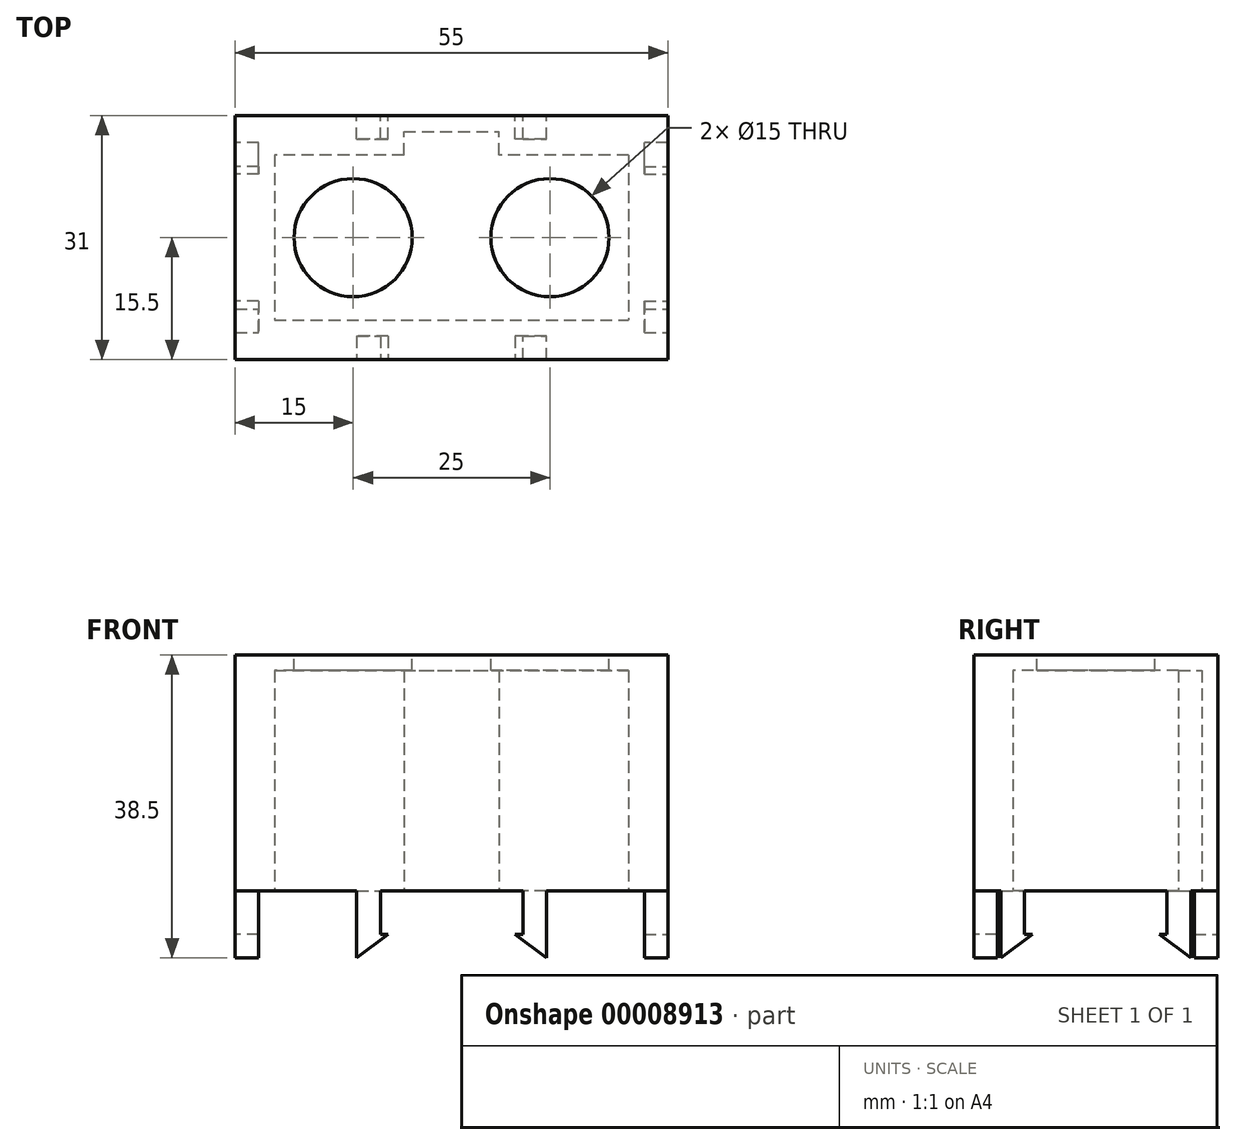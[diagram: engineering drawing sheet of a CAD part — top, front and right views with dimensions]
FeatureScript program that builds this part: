
annotation { "Feature Type Name" : "Feature", "Feature Type Description" : "" }
export const myFeature = defineFeature(function(context is Context, id is Id, definition is map)
    precondition{}
    {
        {
            var Q0;
            Q0=qCreatedBy(makeId("Top.planeOp"),FACE);
            var sketch = newSketch(context, id + "F0", { "sketchPlane" : qUnion([Q0])});
            skLineSegment(sketch, "E0", {"start": v(0, 0) * mm, "end": v(-22, 0) * mm});
            skLineSegment(sketch, "E1", {"start": v(0, 0) * mm, "end": v(22, 0) * mm});
            skLineSegment(sketch, "E2.0", {"start": v(0, 10) * mm, "end": v(-22, 10) * mm, "construction": true});
            skLineSegment(sketch, "E3.0", {"start": v(0, 10) * mm, "end": v(22, 10) * mm, "construction": true});
            skLineSegment(sketch, "E4.0", {"start": v(0, -10) * mm, "end": v(22, -10) * mm, "construction": true});
            skLineSegment(sketch, "E5.0", {"start": v(0, -10) * mm, "end": v(-22, -10) * mm, "construction": true});
            skLineSegment(sketch, "E6", {"start": v(-22, 10) * mm, "end": v(-22, -10) * mm, "construction": true});
            skLineSegment(sketch, "E7", {"start": v(22, 10) * mm, "end": v(22, -10) * mm, "construction": true});
            skLineSegment(sketch, "E8.0", {"start": v(0, 10.5) * mm, "end": v(-22.5, 10.5) * mm});
            skLineSegment(sketch, "E9.0", {"start": v(0, 10.5) * mm, "end": v(23.37, 10.5) * mm});
            skLineSegment(sketch, "E10.0", {"start": v(-22.5, 12.52) * mm, "end": v(-22.5, -12.38) * mm});
            skLineSegment(sketch, "E11.0", {"start": v(22.5, 10.5) * mm, "end": v(22.5, -10.5) * mm});
            skLineSegment(sketch, "E12.0", {"start": v(0, -10.5) * mm, "end": v(23.75, -10.5) * mm});
            skLineSegment(sketch, "E13.0", {"start": v(0, -10.5) * mm, "end": v(-22.5, -10.5) * mm});
            skLineSegment(sketch, "E14.0", {"start": v(-27.5, 15.5) * mm, "end": v(-27.5, -18.22) * mm});
            skLineSegment(sketch, "E15.0", {"start": v(0, 15.5) * mm, "end": v(-27.5, 15.5) * mm});
            skLineSegment(sketch, "E16.0", {"start": v(0, 15.5) * mm, "end": v(27.5, 15.5) * mm});
            skLineSegment(sketch, "E17.0", {"start": v(27.5, 15.5) * mm, "end": v(27.5, -15.5) * mm});
            skLineSegment(sketch, "E18.0", {"start": v(0, -15.5) * mm, "end": v(27.5, -15.5) * mm});
            skLineSegment(sketch, "E19.0", {"start": v(0, -15.5) * mm, "end": v(-27.5, -15.5) * mm});
            skSolve(sketch);
        }
        {
            var Q0;
            {var subQ7=sQuery(id+"F0.wireOp",EDGE,"E8.0");Q0=makeQuery(id+"F0.imprint","IMPRINT",FACE,{"disambiguationData":[TD([[makeQuery(id+"F0.imprint","IMPRINT",EDGE,{"derivedFrom":subQ7}),-1.0]])]});}
            extrude(context, id + "F1", {"entities" : qUnion([Q0]), "depth" : 30 * mm});
        }
        {
            var Q0;
            Q0=makeQuery(id+"F1.opExtrude","CAP_FACE",FACE,{"disambiguationData":[OSD([sQuery(id+"F0.wireOp",EDGE,"E8.0"),sQuery(id+"F0.wireOp",EDGE,"E9.0"),sQuery(id+"F0.wireOp",EDGE,"E10.0"),sQuery(id+"F0.wireOp",EDGE,"E11.0"),sQuery(id+"F0.wireOp",EDGE,"E12.0"),sQuery(id+"F0.wireOp",EDGE,"E13.0"),sQuery(id+"F0.wireOp",EDGE,"E14.0"),sQuery(id+"F0.wireOp",EDGE,"E15.0"),sQuery(id+"F0.wireOp",EDGE,"E16.0"),sQuery(id+"F0.wireOp",EDGE,"E17.0"),sQuery(id+"F0.wireOp",EDGE,"E18.0"),sQuery(id+"F0.wireOp",EDGE,"E19.0")])],"isStart":false});
            var sketch = newSketch(context, id + "F2", { "sketchPlane" : qUnion([Q0])});
            skLineSegment(sketch, "E20", {"start": v(-22.5, 10.5) * mm, "end": v(-22.5, -10.5) * mm});
            skLineSegment(sketch, "E21", {"start": v(-22.5, -10.5) * mm, "end": v(22.5, -10.5) * mm});
            skLineSegment(sketch, "E22", {"start": v(22.5, -10.5) * mm, "end": v(22.5, 10.5) * mm});
            skLineSegment(sketch, "E23", {"start": v(22.5, 10.5) * mm, "end": v(-22.5, 10.5) * mm});
            skSolve(sketch);
        }
        {
            var Q0;
            Q0=makeQuery(id+"F2.imprint","IMPRINT",FACE,{"disambiguationData":[TD([[makeQuery(id+"F2.imprint","IMPRINT",EDGE,{"derivedFrom":sQuery(id+"F2.wireOp",EDGE,"E20")}),1.0]])]});
            extrude(context, id + "F3", {"entities" : qUnion([Q0]), "operationType" : NewBodyOperationType.ADD, "oppositeDirection" : true, "depth" : 2 * mm});
        }
        {
            var Q0;
            {var subQ7=sQuery(id+"F0.wireOp",EDGE,"E8.0");Q0=makeQuery(id+"F0.imprint","IMPRINT",FACE,{"disambiguationData":[TD([[makeQuery(id+"F0.imprint","IMPRINT",EDGE,{"derivedFrom":subQ7}),-1.0]])]});}
            var sketch = newSketch(context, id + "F4", { "sketchPlane" : qUnion([Q0])});
            skLineSegment(sketch, "E24.0", {"start": v(0, 10.5) * mm, "end": v(-22.5, 10.5) * mm});
            skLineSegment(sketch, "E25.0", {"start": v(0, 10.5) * mm, "end": v(23.37, 10.5) * mm});
            skLineSegment(sketch, "E26", {"start": v(0, 10.5) * mm, "end": v(0, 13.5) * mm});
            skPoint(sketch, "E27.orphan", {"position": v(0, 12.52) * mm});
            skLineSegment(sketch, "E28.0", {"start": v(6.05, 10.5) * mm, "end": v(6.05, 13.5) * mm});
            skLineSegment(sketch, "E29.0", {"start": v(-6.05, 10.5) * mm, "end": v(-6.05, 13.5) * mm});
            skLineSegment(sketch, "E30", {"start": v(-6.05, 13.5) * mm, "end": v(6.05, 13.5) * mm});
            skSolve(sketch);
        }
        {
            var Q0;
            {var subQ2=sQuery(id+"F4.wireOp",EDGE,"E26");Q0=makeQuery(id+"F4.imprint","IMPRINT",FACE,{"disambiguationData":[TD([[makeQuery(id+"F4.imprint","IMPRINT",EDGE,{"derivedFrom":subQ2}),1.0]])]});}
            var Q1;
            {var subQ2=sQuery(id+"F4.wireOp",EDGE,"E26");Q1=makeQuery(id+"F4.imprint","IMPRINT",FACE,{"disambiguationData":[TD([[makeQuery(id+"F4.imprint","IMPRINT",EDGE,{"derivedFrom":subQ2}),-1.0]])]});}
            extrude(context, id + "F5", {"entities" : qUnion([Q0, Q1]), "operationType" : NewBodyOperationType.REMOVE, "depth" : 28 * mm});
        }
        {
            var Q0;
            Q0=makeQuery(id+"F3.boolean.opBoolean","MERGE",FACE,{"derivedFrom":[makeQuery(id+"F1.opExtrude","CAP_FACE",FACE,{"disambiguationData":[OSD([sQuery(id+"F0.wireOp",EDGE,"E8.0"),sQuery(id+"F0.wireOp",EDGE,"E9.0"),sQuery(id+"F0.wireOp",EDGE,"E10.0"),sQuery(id+"F0.wireOp",EDGE,"E11.0"),sQuery(id+"F0.wireOp",EDGE,"E12.0"),sQuery(id+"F0.wireOp",EDGE,"E13.0"),sQuery(id+"F0.wireOp",EDGE,"E14.0"),sQuery(id+"F0.wireOp",EDGE,"E15.0"),sQuery(id+"F0.wireOp",EDGE,"E16.0"),sQuery(id+"F0.wireOp",EDGE,"E17.0"),sQuery(id+"F0.wireOp",EDGE,"E18.0"),sQuery(id+"F0.wireOp",EDGE,"E19.0")])],"isStart":false}),makeQuery(id+"F3.opExtrude","CAP_FACE",FACE,{"disambiguationData":[OSD([sQuery(id+"F2.wireOp",EDGE,"E20"),sQuery(id+"F2.wireOp",EDGE,"E21"),sQuery(id+"F2.wireOp",EDGE,"E22"),sQuery(id+"F2.wireOp",EDGE,"E23")])],"isStart":true})]});
            var sketch = newSketch(context, id + "F6", { "sketchPlane" : qUnion([Q0])});
            skLineSegment(sketch, "E31", {"start": v(0, 0) * mm, "end": v(-5, 0) * mm});
            skLineSegment(sketch, "E32", {"start": v(0, 0) * mm, "end": v(5, 0) * mm});
            skLineSegment(sketch, "E33", {"start": v(-5, 0) * mm, "end": v(-12.5, 0) * mm});
            skLineSegment(sketch, "E34", {"start": v(5, 0) * mm, "end": v(12.5, 0) * mm});
            skCircle(sketch, "E35", {"center": v(-12.5, 0) * mm, "radius": 7.5 * mm});
            skCircle(sketch, "E36", {"center": v(12.5, 0) * mm, "radius": 7.5 * mm});
            skSolve(sketch);
        }
        {
            var Q0;
            Q0=makeQuery(id+"F6.imprint","IMPRINT",FACE,{"disambiguationData":[TD([[makeQuery(id+"F6.imprint","IMPRINT",EDGE,{"derivedFrom":sQuery(id+"F6.wireOp",EDGE,"E35")}),1.0]])]});
            var Q1;
            Q1=makeQuery(id+"F6.imprint","IMPRINT",FACE,{"disambiguationData":[TD([[makeQuery(id+"F6.imprint","IMPRINT",EDGE,{"derivedFrom":sQuery(id+"F6.wireOp",EDGE,"E36")}),1.0]])]});
            extrude(context, id + "F7", {"entities" : qUnion([Q0, Q1]), "operationType" : NewBodyOperationType.REMOVE, "oppositeDirection" : true, "depth" : 2 * mm});
        }
        {
            var Q0;
            Q0=makeQuery(id+"F1.opExtrude","CAP_FACE",FACE,{"disambiguationData":[OSD([sQuery(id+"F0.wireOp",EDGE,"E8.0"),sQuery(id+"F0.wireOp",EDGE,"E9.0"),sQuery(id+"F0.wireOp",EDGE,"E10.0"),sQuery(id+"F0.wireOp",EDGE,"E11.0"),sQuery(id+"F0.wireOp",EDGE,"E12.0"),sQuery(id+"F0.wireOp",EDGE,"E13.0"),sQuery(id+"F0.wireOp",EDGE,"E14.0"),sQuery(id+"F0.wireOp",EDGE,"E15.0"),sQuery(id+"F0.wireOp",EDGE,"E16.0"),sQuery(id+"F0.wireOp",EDGE,"E17.0"),sQuery(id+"F0.wireOp",EDGE,"E18.0"),sQuery(id+"F0.wireOp",EDGE,"E19.0")])],"isStart":true});
            var sketch = newSketch(context, id + "F8", { "sketchPlane" : qUnion([Q0])});
            skLineSegment(sketch, "E37", {"start": v(0, 0) * mm, "end": v(-27.5, 0) * mm});
            skLineSegment(sketch, "E38", {"start": v(0, 0) * mm, "end": v(27.5, 0) * mm});
            skLineSegment(sketch, "E39", {"start": v(0, 0) * mm, "end": v(0, 15.5) * mm});
            skLineSegment(sketch, "E40", {"start": v(0, 0) * mm, "end": v(0, -15.5) * mm});
            skLineSegment(sketch, "E41", {"start": v(-27.5, 0) * mm, "end": v(-27.5, 9.05) * mm});
            skLineSegment(sketch, "E42", {"start": v(-27.5, 0) * mm, "end": v(-27.5, -9.05) * mm});
            skLineSegment(sketch, "E43", {"start": v(0, 15.5) * mm, "end": v(9.05, 15.5) * mm});
            skLineSegment(sketch, "E44", {"start": v(0, 15.5) * mm, "end": v(-9.05, 15.5) * mm});
            skLineSegment(sketch, "E45", {"start": v(27.5, 0) * mm, "end": v(27.5, 9.05) * mm});
            skLineSegment(sketch, "E46", {"start": v(27.5, 0) * mm, "end": v(27.5, -9.05) * mm});
            skLineSegment(sketch, "E47", {"start": v(0, -15.5) * mm, "end": v(9.05, -15.5) * mm});
            skLineSegment(sketch, "E48", {"start": v(0, -15.5) * mm, "end": v(-9.05, -15.5) * mm});
            skPoint(sketch, "E49.orphan", {"position": v(6.05, -15.5) * mm});
            skLineSegment(sketch, "E50.0", {"start": v(24.5, 0) * mm, "end": v(24.5, -9.05) * mm});
            skLineSegment(sketch, "E50.1", {"start": v(24.5, 0) * mm, "end": v(24.5, 9.05) * mm});
            skLineSegment(sketch, "E51.0", {"start": v(0, -12.5) * mm, "end": v(9.05, -12.5) * mm});
            skLineSegment(sketch, "E51.1", {"start": v(0, -12.5) * mm, "end": v(-9.05, -12.5) * mm});
            skLineSegment(sketch, "E52.0", {"start": v(-24.5, 0) * mm, "end": v(-24.5, 9.05) * mm});
            skLineSegment(sketch, "E52.1", {"start": v(-24.5, 0) * mm, "end": v(-24.5, -9.05) * mm});
            skLineSegment(sketch, "E53.0", {"start": v(0, 12.5) * mm, "end": v(-9.05, 12.5) * mm});
            skLineSegment(sketch, "E53.1", {"start": v(0, 12.5) * mm, "end": v(9.05, 12.5) * mm});
            skLineSegment(sketch, "E54", {"start": v(-27.5, 9.05) * mm, "end": v(-24.5, 9.05) * mm});
            skLineSegment(sketch, "E55", {"start": v(-24.5, -9.05) * mm, "end": v(-27.5, -9.05) * mm});
            skLineSegment(sketch, "E56", {"start": v(-9.05, 12.5) * mm, "end": v(-9.05, 15.5) * mm});
            skLineSegment(sketch, "E57", {"start": v(9.05, 15.5) * mm, "end": v(9.05, 12.5) * mm});
            skLineSegment(sketch, "E58", {"start": v(24.5, 9.05) * mm, "end": v(27.5, 9.05) * mm});
            skLineSegment(sketch, "E59", {"start": v(27.5, -9.05) * mm, "end": v(24.5, -9.05) * mm});
            skLineSegment(sketch, "E60", {"start": v(9.05, -12.5) * mm, "end": v(9.05, -15.5) * mm});
            skLineSegment(sketch, "E61", {"start": v(-9.05, -12.5) * mm, "end": v(-9.05, -15.5) * mm});
            skLineSegment(sketch, "E62.0", {"start": v(-24.5, -12.05) * mm, "end": v(-27.5, -12.05) * mm});
            skLineSegment(sketch, "E63.0", {"start": v(-27.5, 12.05) * mm, "end": v(-24.5, 12.05) * mm});
            skLineSegment(sketch, "E64.0", {"start": v(-12.05, 12.5) * mm, "end": v(-12.05, 15.5) * mm});
            skLineSegment(sketch, "E65.0", {"start": v(12.05, 15.5) * mm, "end": v(12.05, 12.5) * mm});
            skLineSegment(sketch, "E66.0", {"start": v(24.5, 12.05) * mm, "end": v(27.5, 12.05) * mm});
            skLineSegment(sketch, "E67.0", {"start": v(27.5, -12.05) * mm, "end": v(24.5, -12.05) * mm});
            skLineSegment(sketch, "E68.0", {"start": v(12.05, -12.5) * mm, "end": v(12.05, -15.5) * mm});
            skLineSegment(sketch, "E69.0", {"start": v(-12.05, -12.5) * mm, "end": v(-12.05, -15.5) * mm});
            skLineSegment(sketch, "E70", {"start": v(-24.5, -9.05) * mm, "end": v(-24.5, -12.05) * mm});
            skLineSegment(sketch, "E71", {"start": v(-27.5, -9.05) * mm, "end": v(-27.5, -12.05) * mm});
            skLineSegment(sketch, "E72", {"start": v(-27.5, 12.05) * mm, "end": v(-27.5, 9.05) * mm});
            skLineSegment(sketch, "E73", {"start": v(-24.5, 12.05) * mm, "end": v(-24.5, 9.05) * mm});
            skLineSegment(sketch, "E74", {"start": v(-12.05, 15.5) * mm, "end": v(-9.05, 15.5) * mm});
            skLineSegment(sketch, "E75", {"start": v(-12.05, 12.5) * mm, "end": v(-9.05, 12.5) * mm});
            skLineSegment(sketch, "E76", {"start": v(9.05, 15.5) * mm, "end": v(12.05, 15.5) * mm});
            skLineSegment(sketch, "E77", {"start": v(9.05, 12.5) * mm, "end": v(12.05, 12.5) * mm});
            skLineSegment(sketch, "E78", {"start": v(24.5, 12.05) * mm, "end": v(24.5, 9.05) * mm});
            skLineSegment(sketch, "E79", {"start": v(27.5, 12.05) * mm, "end": v(27.5, 9.05) * mm});
            skLineSegment(sketch, "E80", {"start": v(24.5, -9.05) * mm, "end": v(24.5, -12.05) * mm});
            skLineSegment(sketch, "E81", {"start": v(27.5, -9.05) * mm, "end": v(27.5, -12.05) * mm});
            skLineSegment(sketch, "E82", {"start": v(9.05, -12.5) * mm, "end": v(12.05, -12.5) * mm});
            skLineSegment(sketch, "E83", {"start": v(9.05, -15.5) * mm, "end": v(12.05, -15.5) * mm});
            skLineSegment(sketch, "E84", {"start": v(-12.05, -12.5) * mm, "end": v(-9.05, -12.5) * mm});
            skLineSegment(sketch, "E85", {"start": v(-12.05, -15.5) * mm, "end": v(-9.05, -15.5) * mm});
            skSolve(sketch);
        }
        {
            var Q0;
            Q0=makeQuery(id+"F8.imprint","IMPRINT",FACE,{"disambiguationData":[TD([[makeQuery(id+"F8.imprint","IMPRINT",EDGE,{"derivedFrom":sQuery(id+"F8.wireOp",EDGE,"E54")}),1.0]])]});
            var Q1;
            Q1=makeQuery(id+"F8.imprint","IMPRINT",FACE,{"disambiguationData":[TD([[makeQuery(id+"F8.imprint","IMPRINT",EDGE,{"derivedFrom":sQuery(id+"F8.wireOp",EDGE,"E55")}),1.0]])]});
            var Q2;
            Q2=makeQuery(id+"F8.imprint","IMPRINT",FACE,{"disambiguationData":[TD([[makeQuery(id+"F8.imprint","IMPRINT",EDGE,{"derivedFrom":sQuery(id+"F8.wireOp",EDGE,"E61")}),-1.0]])]});
            var Q3;
            Q3=makeQuery(id+"F8.imprint","IMPRINT",FACE,{"disambiguationData":[TD([[makeQuery(id+"F8.imprint","IMPRINT",EDGE,{"derivedFrom":sQuery(id+"F8.wireOp",EDGE,"E60")}),1.0]])]});
            var Q4;
            Q4=makeQuery(id+"F8.imprint","IMPRINT",FACE,{"disambiguationData":[TD([[makeQuery(id+"F8.imprint","IMPRINT",EDGE,{"derivedFrom":sQuery(id+"F8.wireOp",EDGE,"E56")}),1.0]])]});
            var Q5;
            Q5=makeQuery(id+"F8.imprint","IMPRINT",FACE,{"disambiguationData":[TD([[makeQuery(id+"F8.imprint","IMPRINT",EDGE,{"derivedFrom":sQuery(id+"F8.wireOp",EDGE,"E57")}),1.0]])]});
            var Q6;
            Q6=makeQuery(id+"F8.imprint","IMPRINT",FACE,{"disambiguationData":[TD([[makeQuery(id+"F8.imprint","IMPRINT",EDGE,{"derivedFrom":sQuery(id+"F8.wireOp",EDGE,"E58")}),1.0]])]});
            var Q7;
            Q7=makeQuery(id+"F8.imprint","IMPRINT",FACE,{"disambiguationData":[TD([[makeQuery(id+"F8.imprint","IMPRINT",EDGE,{"derivedFrom":sQuery(id+"F8.wireOp",EDGE,"E59")}),1.0]])]});
            extrude(context, id + "F9", {"entities" : qUnion([Q0, Q1, Q2, Q3, Q4, Q5, Q6, Q7]), "operationType" : NewBodyOperationType.ADD, "depth" : 8.5 * mm});
        }
        {
            var Q0;
            Q0=makeQuery(id+"F9.boolean.opBoolean","MERGE",FACE,{"derivedFrom":[makeQuery(id+"F1.opExtrude","SWEPT_FACE",FACE,{"disambiguationData":[OSD([sQuery(id+"F0.wireOp",EDGE,"E14.0")])]}),makeQuery(id+"F9.opExtrude","SWEPT_FACE",FACE,{"disambiguationData":[OSD([sQuery(id+"F8.wireOp",EDGE,"E71")])]}),makeQuery(id+"F9.opExtrude","SWEPT_FACE",FACE,{"disambiguationData":[OSD([sQuery(id+"F8.wireOp",EDGE,"E72")])]})]});
            var sketch = newSketch(context, id + "F10", { "sketchPlane" : qUnion([Q0])});
            skLineSegment(sketch, "E86.0", {"start": v(9.05, -6.5) * mm, "end": v(12.05, -6.5) * mm, "construction": true});
            skLineSegment(sketch, "E87.0", {"start": v(8.05, -5.5) * mm, "end": v(12.05, -5.5) * mm});
            skLineSegment(sketch, "E88.0", {"start": v(-12.05, -6.5) * mm, "end": v(-9.05, -6.5) * mm, "construction": true});
            skLineSegment(sketch, "E89.0", {"start": v(-12.05, -5.5) * mm, "end": v(-8.05, -5.5) * mm});
            skLineSegment(sketch, "E90.0", {"start": v(8.05, -8.5) * mm, "end": v(8.05, 0) * mm});
            skLineSegment(sketch, "E91.0", {"start": v(-8.05, -8.5) * mm, "end": v(-8.05, 0) * mm});
            skLineSegment(sketch, "E92", {"start": v(12.05, -8.5) * mm, "end": v(8.05, -5.5) * mm});
            skLineSegment(sketch, "E93", {"start": v(-12.05, -8.5) * mm, "end": v(-8.05, -5.5) * mm});
            skSolve(sketch);
        }
        {
            var Q0;
            {var subQ0=sQuery(id+"F8.wireOp",EDGE,"E72");var subQ4=makeQuery(id+"F9.opExtrude","CAP_EDGE",EDGE,{"disambiguationData":[OSD([subQ0])],"isStart":false});Q0=makeQuery(id+"F10.imprint","IMPRINT",FACE,{"disambiguationData":[TD([[makeQuery(id+"F10.imprint","IMPRINT",EDGE,{"derivedFrom":subQ4}),1.0]])]});}
            var Q1;
            {var subQ0=sQuery(id+"F8.wireOp",EDGE,"E71");var subQ4=makeQuery(id+"F9.opExtrude","CAP_EDGE",EDGE,{"disambiguationData":[OSD([subQ0])],"isStart":false});Q1=makeQuery(id+"F10.imprint","IMPRINT",FACE,{"disambiguationData":[TD([[makeQuery(id+"F10.imprint","IMPRINT",EDGE,{"derivedFrom":subQ4}),1.0]])]});}
            extrude(context, id + "F11", {"entities" : qUnion([Q0, Q1]), "operationType" : NewBodyOperationType.REMOVE, "oppositeDirection" : true, "depth" : 60 * mm});
        }
        {
            var Q0;
            {var subQ1=sQuery(id+"F10.wireOp",EDGE,"E87.0");var subQ3=sQuery(id+"F10.wireOp",EDGE,"E92");var subQ5=makeQuery(id+"F10.imprint","INTERSECT",VERTEX,{"derivedFrom":[subQ1,sQuery(id+"F10.wireOp",EDGE,"E90.0"),subQ3]});Q0=makeQuery(id+"F10.imprint","IMPRINT",FACE,{"disambiguationData":[TD([[makeQuery(id+"F10.imprint","IMPRINT",EDGE,{"disambiguationData":[TD([[subQ5,-1.0]])],"derivedFrom":subQ1}),-1.0]])]});}
            var Q1;
            {var subQ1=sQuery(id+"F10.wireOp",EDGE,"E89.0");var subQ3=sQuery(id+"F10.wireOp",EDGE,"E93");var subQ5=makeQuery(id+"F10.imprint","INTERSECT",VERTEX,{"derivedFrom":[subQ1,sQuery(id+"F10.wireOp",EDGE,"E91.0"),subQ3]});Q1=makeQuery(id+"F10.imprint","IMPRINT",FACE,{"disambiguationData":[TD([[makeQuery(id+"F10.imprint","IMPRINT",EDGE,{"disambiguationData":[TD([[subQ5,1.0]])],"derivedFrom":subQ1}),-1.0]])]});}
            extrude(context, id + "F12", {"entities" : qUnion([Q0, Q1]), "operationType" : NewBodyOperationType.ADD, "oppositeDirection" : true, "depth" : 3 * mm});
        }
        {
            var Q0;
            Q0=makeQuery(id+"F9.boolean.opBoolean","MERGE",FACE,{"derivedFrom":[makeQuery(id+"F1.opExtrude","SWEPT_FACE",FACE,{"disambiguationData":[OSD([sQuery(id+"F0.wireOp",EDGE,"E17.0")])]}),makeQuery(id+"F9.opExtrude","SWEPT_FACE",FACE,{"disambiguationData":[OSD([sQuery(id+"F8.wireOp",EDGE,"E79")])]}),makeQuery(id+"F9.opExtrude","SWEPT_FACE",FACE,{"disambiguationData":[OSD([sQuery(id+"F8.wireOp",EDGE,"E81")])]})]});
            var sketch = newSketch(context, id + "F13", { "sketchPlane" : qUnion([Q0])});
            skLineSegment(sketch, "E94", {"start": v(12.05, -8.5) * mm, "end": v(7.95, -8.5) * mm});
            skLineSegment(sketch, "E95.0", {"start": v(8.05, -8.5) * mm, "end": v(8.05, 0) * mm});
            skLineSegment(sketch, "E96.0", {"start": v(9.05, -8.5) * mm, "end": v(9.05, 0) * mm});
            skLineSegment(sketch, "E97.0", {"start": v(12.05, -5.5) * mm, "end": v(8.05, -5.5) * mm});
            skLineSegment(sketch, "E98", {"start": v(12.05, -8.5) * mm, "end": v(8.05, -5.5) * mm});
            skLineSegment(sketch, "E99", {"start": v(-12.05, -8.5) * mm, "end": v(-7.05, -8.5) * mm});
            skLineSegment(sketch, "E100.0", {"start": v(-8.05, -6.25) * mm, "end": v(-8.05, 0) * mm});
            skLineSegment(sketch, "E101.0", {"start": v(-9.05, -6.25) * mm, "end": v(-9.05, 0) * mm});
            skLineSegment(sketch, "E102.0", {"start": v(-12.05, -5.5) * mm, "end": v(-8.05, -5.5) * mm});
            skLineSegment(sketch, "E103", {"start": v(-12.05, -8.5) * mm, "end": v(-8.05, -5.5) * mm});
            skSolve(sketch);
        }
        {
            var Q0;
            {var subQ0=sQuery(id+"F13.wireOp",EDGE,"E98");var subQ3=sQuery(id+"F13.wireOp",EDGE,"E96.0");var subQ4=makeQuery(id+"F13.imprint","INTERSECT",VERTEX,{"derivedFrom":[subQ3,subQ0]});Q0=makeQuery(id+"F13.imprint","IMPRINT",FACE,{"disambiguationData":[TD([[makeQuery(id+"F13.imprint","IMPRINT",EDGE,{"disambiguationData":[TD([[subQ4,-1.0]])],"derivedFrom":subQ3}),1.0]])]});}
            var Q1;
            {var subQ0=sQuery(id+"F13.wireOp",EDGE,"E103");var subQ3=sQuery(id+"F13.wireOp",EDGE,"E101.0");var subQ4=makeQuery(id+"F13.imprint","INTERSECT",VERTEX,{"derivedFrom":[subQ3,subQ0]});Q1=makeQuery(id+"F13.imprint","IMPRINT",FACE,{"disambiguationData":[TD([[makeQuery(id+"F13.imprint","IMPRINT",EDGE,{"disambiguationData":[TD([[subQ4,-1.0]])],"derivedFrom":subQ3}),-1.0]])]});}
            extrude(context, id + "F14", {"entities" : qUnion([Q0, Q1]), "operationType" : NewBodyOperationType.ADD, "oppositeDirection" : true, "depth" : 3 * mm});
        }
        {
            var Q0;
            Q0=makeQuery(id+"F9.boolean.opBoolean","MERGE",FACE,{"derivedFrom":[makeQuery(id+"F1.opExtrude","SWEPT_FACE",FACE,{"disambiguationData":[OSD([sQuery(id+"F0.wireOp",EDGE,"E18.0"),sQuery(id+"F0.wireOp",EDGE,"E19.0")])]}),makeQuery(id+"F9.opExtrude","SWEPT_FACE",FACE,{"disambiguationData":[OSD([sQuery(id+"F8.wireOp",EDGE,"E74")])]}),makeQuery(id+"F9.opExtrude","SWEPT_FACE",FACE,{"disambiguationData":[OSD([sQuery(id+"F8.wireOp",EDGE,"E76")])]})]});
            var sketch = newSketch(context, id + "F15", { "sketchPlane" : qUnion([Q0])});
            skLineSegment(sketch, "E104.0", {"start": v(12.05, -6.5) * mm, "end": v(9.05, -6.5) * mm, "construction": true});
            skLineSegment(sketch, "E105.0", {"start": v(12.05, -5.5) * mm, "end": v(8.05, -5.5) * mm});
            skLineSegment(sketch, "E106.0", {"start": v(-9.05, -6.5) * mm, "end": v(-12.05, -6.5) * mm, "construction": true});
            skLineSegment(sketch, "E107.0", {"start": v(-8.05, -5.5) * mm, "end": v(-12.05, -5.5) * mm});
            skLineSegment(sketch, "E108.0", {"start": v(8.05, -8.5) * mm, "end": v(8.05, 0) * mm});
            skLineSegment(sketch, "E109.0", {"start": v(-8.05, -8.5) * mm, "end": v(-8.05, 0) * mm});
            skLineSegment(sketch, "E110", {"start": v(12.05, -8.5) * mm, "end": v(8.05, -5.5) * mm});
            skLineSegment(sketch, "E111", {"start": v(-8.05, -5.5) * mm, "end": v(-12.05, -8.5) * mm});
            skSolve(sketch);
        }
        {
            var Q0;
            Q0 = qSketchRegion(id + "F15", true);
            var Q1;
            {var subQ0=sQuery(id+"F8.wireOp",EDGE,"E76");var subQ4=makeQuery(id+"F9.opExtrude","CAP_EDGE",EDGE,{"disambiguationData":[OSD([subQ0])],"isStart":false});Q1=makeQuery(id+"F15.imprint","IMPRINT",FACE,{"disambiguationData":[TD([[makeQuery(id+"F15.imprint","IMPRINT",EDGE,{"derivedFrom":subQ4}),-1.0]])]});}
            var Q2;
            {var subQ0=sQuery(id+"F8.wireOp",EDGE,"E74");var subQ4=makeQuery(id+"F9.opExtrude","CAP_EDGE",EDGE,{"disambiguationData":[OSD([subQ0])],"isStart":false});Q2=makeQuery(id+"F15.imprint","IMPRINT",FACE,{"disambiguationData":[TD([[makeQuery(id+"F15.imprint","IMPRINT",EDGE,{"derivedFrom":subQ4}),-1.0]])]});}
            extrude(context, id + "F16", {"entities" : qUnion([Q0, Q1, Q2]), "operationType" : NewBodyOperationType.REMOVE, "oppositeDirection" : true, "depth" : 35.67 * mm});
        }
        {
            var Q0;
            {var subQ1=sQuery(id+"F15.wireOp",EDGE,"E105.0");var subQ3=sQuery(id+"F15.wireOp",EDGE,"E110");var subQ5=makeQuery(id+"F15.imprint","INTERSECT",VERTEX,{"derivedFrom":[subQ1,sQuery(id+"F15.wireOp",EDGE,"E108.0"),subQ3]});Q0=makeQuery(id+"F15.imprint","IMPRINT",FACE,{"disambiguationData":[TD([[makeQuery(id+"F15.imprint","IMPRINT",EDGE,{"disambiguationData":[TD([[subQ5,1.0]])],"derivedFrom":subQ1}),1.0]])]});}
            var Q1;
            {var subQ1=sQuery(id+"F15.wireOp",EDGE,"E107.0");var subQ3=sQuery(id+"F15.wireOp",EDGE,"E111");var subQ5=makeQuery(id+"F15.imprint","INTERSECT",VERTEX,{"derivedFrom":[subQ1,sQuery(id+"F15.wireOp",EDGE,"E109.0"),subQ3]});Q1=makeQuery(id+"F15.imprint","IMPRINT",FACE,{"disambiguationData":[TD([[makeQuery(id+"F15.imprint","IMPRINT",EDGE,{"disambiguationData":[TD([[subQ5,-1.0]])],"derivedFrom":subQ1}),1.0]])]});}
            extrude(context, id + "F17", {"entities" : qUnion([Q0, Q1]), "operationType" : NewBodyOperationType.ADD, "oppositeDirection" : true, "depth" : 3 * mm});
        }
        {
            var Q0;
            Q0=makeQuery(id+"F9.boolean.opBoolean","MERGE",FACE,{"derivedFrom":[makeQuery(id+"F1.opExtrude","SWEPT_FACE",FACE,{"disambiguationData":[OSD([sQuery(id+"F0.wireOp",EDGE,"E15.0"),sQuery(id+"F0.wireOp",EDGE,"E16.0")])]}),makeQuery(id+"F9.opExtrude","SWEPT_FACE",FACE,{"disambiguationData":[OSD([sQuery(id+"F8.wireOp",EDGE,"E83")])]}),makeQuery(id+"F9.opExtrude","SWEPT_FACE",FACE,{"disambiguationData":[OSD([sQuery(id+"F8.wireOp",EDGE,"E85")])]})]});
            var sketch = newSketch(context, id + "F18", { "sketchPlane" : qUnion([Q0])});
            skLineSegment(sketch, "E112.0", {"start": v(8.05, -8.5) * mm, "end": v(8.05, 0) * mm});
            skLineSegment(sketch, "E113.0", {"start": v(-8.05, -8.5) * mm, "end": v(-8.05, 0) * mm});
            skLineSegment(sketch, "E114", {"start": v(12.05, -8.5) * mm, "end": v(8.05, -8.5) * mm});
            skLineSegment(sketch, "E115", {"start": v(-12.05, -8.5) * mm, "end": v(-8.05, -8.5) * mm});
            skLineSegment(sketch, "E116.0", {"start": v(12.05, -5.5) * mm, "end": v(8.05, -5.5) * mm});
            skLineSegment(sketch, "E117.0", {"start": v(-12.05, -5.5) * mm, "end": v(-8.05, -5.5) * mm});
            skLineSegment(sketch, "E118", {"start": v(12.05, -8.5) * mm, "end": v(8.05, -5.5) * mm});
            skLineSegment(sketch, "E119", {"start": v(-12.05, -8.5) * mm, "end": v(-8.05, -5.5) * mm});
            skSolve(sketch);
        }
        {
            var Q0;
            {var subQ1=sQuery(id+"F18.wireOp",EDGE,"E116.0");var subQ3=sQuery(id+"F18.wireOp",EDGE,"E118");var subQ5=makeQuery(id+"F18.imprint","INTERSECT",VERTEX,{"derivedFrom":[sQuery(id+"F18.wireOp",EDGE,"E112.0"),subQ1,subQ3]});Q0=makeQuery(id+"F18.imprint","IMPRINT",FACE,{"disambiguationData":[TD([[makeQuery(id+"F18.imprint","IMPRINT",EDGE,{"disambiguationData":[TD([[subQ5,1.0]])],"derivedFrom":subQ1}),1.0]])]});}
            var Q1;
            {var subQ1=sQuery(id+"F18.wireOp",EDGE,"E117.0");var subQ3=sQuery(id+"F18.wireOp",EDGE,"E119");var subQ5=makeQuery(id+"F18.imprint","INTERSECT",VERTEX,{"derivedFrom":[sQuery(id+"F18.wireOp",EDGE,"E113.0"),subQ1,subQ3]});Q1=makeQuery(id+"F18.imprint","IMPRINT",FACE,{"disambiguationData":[TD([[makeQuery(id+"F18.imprint","IMPRINT",EDGE,{"disambiguationData":[TD([[subQ5,1.0]])],"derivedFrom":subQ1}),-1.0]])]});}
            extrude(context, id + "F19", {"entities" : qUnion([Q0, Q1]), "operationType" : NewBodyOperationType.ADD, "oppositeDirection" : true, "depth" : 3 * mm});
        }
    });
